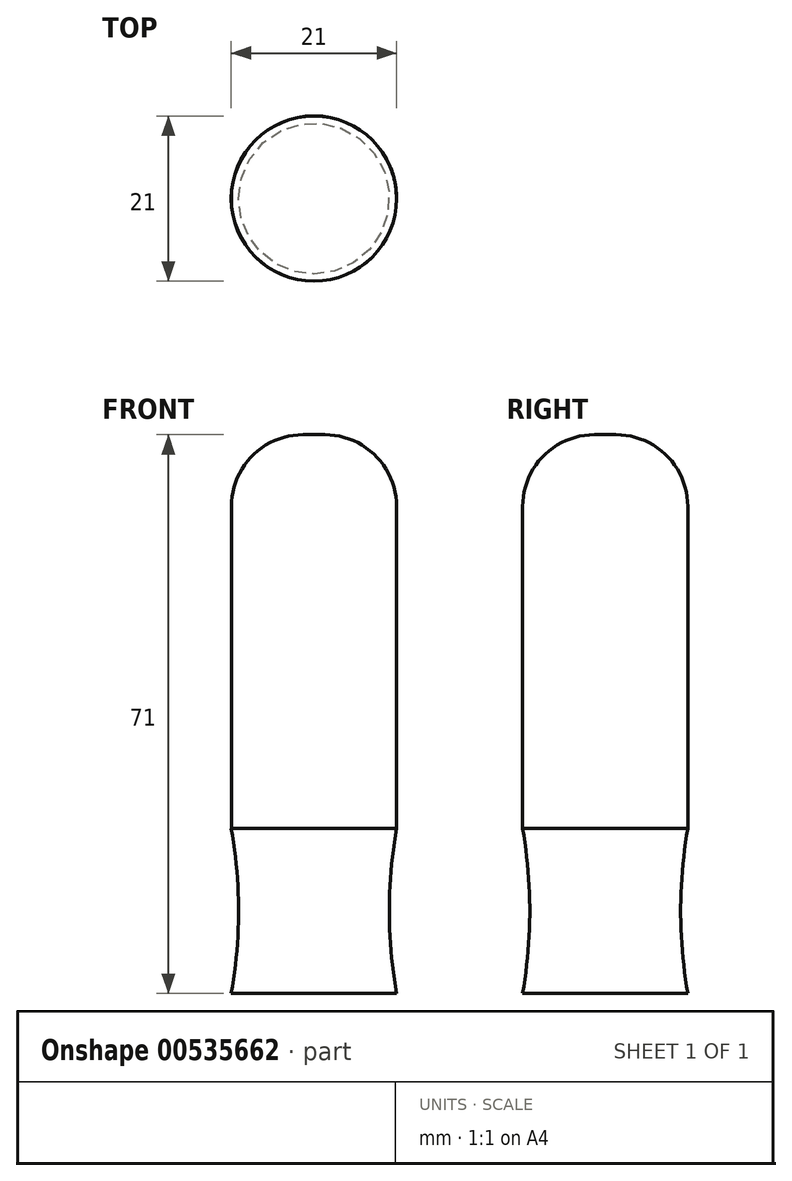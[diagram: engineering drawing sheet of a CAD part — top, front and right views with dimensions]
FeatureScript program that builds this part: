
annotation { "Feature Type Name" : "Feature", "Feature Type Description" : "" }
export const myFeature = defineFeature(function(context is Context, id is Id, definition is map)
    precondition{}
    {
        {
            var Q0;
            Q0=qCreatedBy(makeId("Front.planeOp"),FACE);
            var sketch = newSketch(context, id + "F0", { "sketchPlane" : qUnion([Q0])});
            skLineSegment(sketch, "E0", {"start": v(0, 0) * mm, "end": v(0, 116.6) * mm, "construction": true});
            skLineSegment(sketch, "E1", {"start": v(0, 0) * mm, "end": v(-10.5, 0) * mm});
            skLineSegment(sketch, "E2", {"start": v(0, 21) * mm, "end": v(-10.5, 21) * mm});
            skArc(sketch, "E3", {"start": v(-10.5, 0) * mm, "mid": v(-9.58, 10.5) * mm, "end": v(-10.5, 21) * mm});
            skLineSegment(sketch, "E4", {"start": v(0, 21) * mm, "end": v(0, 0) * mm});
            skSolve(sketch);
        }
        {
            var Q0;
            Q0 = qSketchRegion(id + "F0", true);
            var Q1;
            Q1=sQuery(id+"F0.wireOp",EDGE,"E0");
            revolve(context, id + "F1", {"entities" : qUnion([Q0]), "axis" : qUnion([Q1]), "revolveType" : RevolveType.FULL});
        }
        {
            var Q0;
            Q0=makeQuery(id+"F1.opRevolve","SWEPT_FACE",FACE,{"disambiguationData":[OSD([sQuery(id+"F0.wireOp",EDGE,"E2")])]});
            var sketch = newSketch(context, id + "F2", { "sketchPlane" : qUnion([Q0])});
            skCircle(sketch, "E5", {"center": v(0, 0) * mm, "radius": 10.5 * mm});
            skSolve(sketch);
        }
        {
            var Q0;
            Q0 = qSketchRegion(id + "F2", true);
            extrude(context, id + "F3", {"entities" : qUnion([Q0]), "operationType" : NewBodyOperationType.ADD, "depth" : 50 * mm, "offsetDistance" : 25 * mm});
        }
        {
            var Q0;
            Q0=makeQuery(id+"F3.opExtrude","CAP_EDGE",EDGE,{"disambiguationData":[OSD([sQuery(id+"F2.wireOp",EDGE,"E5")])],"isStart":false});
            fillet(context, id + "F4", {"entities" : qUnion([Q0]), "radius" : 9.1 * mm, "tangentPropagation" : true, "allowEdgeOverflow" : false});
        }
    });
